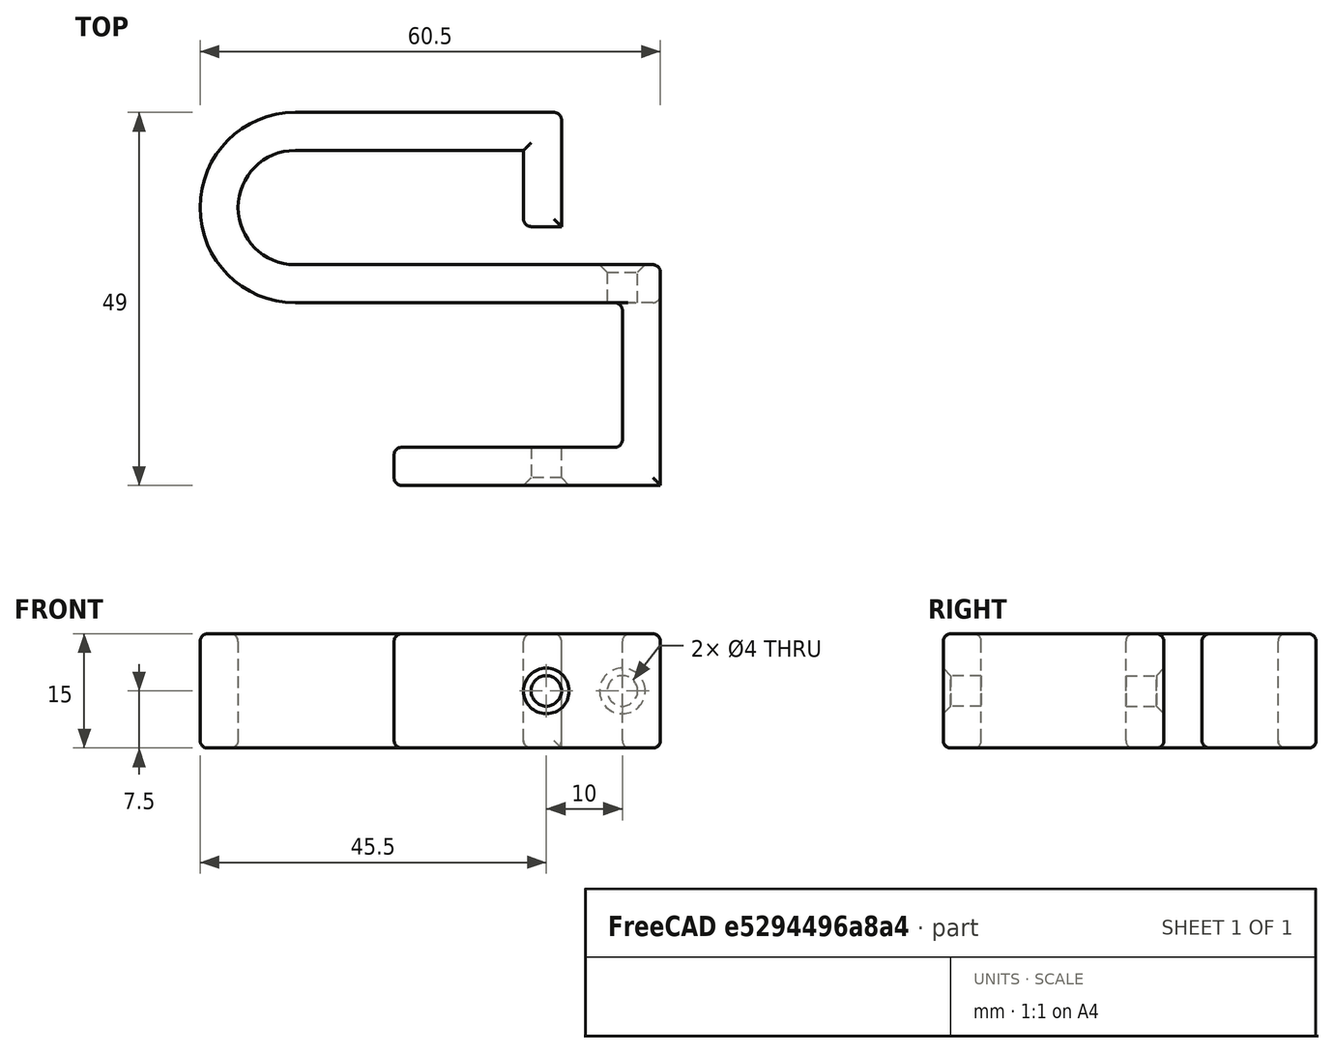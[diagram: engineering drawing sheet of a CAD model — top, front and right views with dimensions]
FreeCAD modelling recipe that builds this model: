
FCSTD DOCUMENT  (FreeCAD 0.21R33771 (Git))
Label: CableClip
License: All rights reserved
LicenseURL: http://en.wikipedia.org/wiki/All_rights_reserved
objects: Sketcher::SketchObject×4, PartDesign::Pad×2, PartDesign::Pocket×2, PartDesign::Chamfer×2, PartDesign::Fillet×2, PartDesign::Body×2, Mesh::Feature×2
note: 22 computed .brp shape members not serialized (recipe doc carries the construction recipe); baked Part::Feature solids carry a one-line shape summary decoded from their .brp

FEATURE [Sketcher::SketchObject] Sketch
  FullyConstrained = true
  MapMode = 5
  Support = -> [XY_Plane]
  sketch-geometry (10):
    g0: LineSegment StartX=13 StartY=-10 StartZ=0 EndX=-35 EndY=-10 EndZ=0
    g1: LineSegment StartX=-35 StartY=15 StartZ=0 EndX=0 EndY=15 EndZ=0
    g2: LineSegment StartX=0 StartY=15 StartZ=0 EndX=0 EndY=0 EndZ=0
    g3: ArcOfCircle CenterX=-35 CenterY=2.5 CenterZ=0 NormalX=0 NormalY=0 NormalZ=1 AngleXU=0 Radius=12.5 StartAngle=1.5708 EndAngle=4.71239
    g4: LineSegment StartX=0 StartY=0 StartZ=0 EndX=-5 EndY=0 EndZ=0
    g5: LineSegment StartX=-5 StartY=0 StartZ=0 EndX=-5 EndY=10 EndZ=0
    g6: LineSegment StartX=-5 StartY=10 StartZ=0 EndX=-35 EndY=10 EndZ=0
    g7: LineSegment StartX=-35 StartY=-5 StartZ=0 EndX=13 EndY=-5 EndZ=0
    g8: LineSegment StartX=13 StartY=-5 StartZ=0 EndX=13 EndY=-10 EndZ=0
    g9: ArcOfCircle CenterX=-35 CenterY=2.5 CenterZ=0 NormalX=0 NormalY=0 NormalZ=1 AngleXU=0 Radius=7.5 StartAngle=1.5708 EndAngle=4.71239
  constraints (31):
    c: Horizontal(g0)
    c: Horizontal(g1)
    c: Coincident(g1,g2)
    c: Coincident(g3,g0)
    c: DistanceX(g0,g0) = 48
    c: DistanceX(g1,g1) = 35
    c: Coincident(g3,g1)
    c: Diameter(g3) = 25
    c: Vertical(g1,g3)
    c: Vertical(g3,g0)
    c: Vertical(g2)
    c: DistanceY(g2,g2) = 15
    c: Coincident(g4,g5)
    c: Coincident(g5,g6)
    c: Horizontal(g6)
    c: Horizontal(g7)
    c: Coincident(g7,g8)
    c: Coincident(g8,g0)
    c: Vertical(g8)
    c: Coincident(g9,g6)
    c: Diameter(g9) = 15
    c: Coincident(g9,g7)
    c: Coincident(g2,g-1)
    c: Coincident(g4,g2)
    c: Horizontal(g4)
    c: DistanceX(g4,g4) = 5
    c: Vertical(g5,g4)
    c: DistanceY(g5,g1) = 5
    c: DistanceY(g0,g7) = 5
    c: Vertical(g0,g7)
    c: Vertical(g7,g6)
FEATURE [PartDesign::Pad] Pad
  Direction = (0,0,1)
  Length = 15
  Length2 = 10
  Profile = -> Sketch
  ReferenceAxis = -> Sketch [N_Axis]
  Type = 0
FEATURE [Sketcher::SketchObject] Sketch001
  ExternalGeometry = -> [Pad]
  FullyConstrained = true
  MapMode = 5
  Placement = pos=(0,-5,0) rot=(0,0.707107,0.707107;3.14159rad)
  Support = -> [Pad]
  sketch-geometry (1):
    g0: Circle CenterX=-8 CenterY=7.5 CenterZ=0 NormalX=0 NormalY=0 NormalZ=1 AngleXU=0 Radius=2
  constraints (3):
    c: Diameter(g0) = 4
    c: DistanceY(g-3,g0) = 7.5
    c: DistanceX(g-3,g0) = 5
FEATURE [PartDesign::Pocket] Pocket
  BaseFeature = -> Pad
  Direction = (0,-1,2e-16)
  Length = 5
  Length2 = 5
  Profile = -> Sketch001
  ReferenceAxis = -> Sketch001 [N_Axis]
  Type = 0
FEATURE [PartDesign::Chamfer] Chamfer
  Angle = 45
  Base = -> Pocket [Edge27]
  BaseFeature = -> Pocket
  ChamferType = 0
  FlipDirection = false
  Size = 1
  Size2 = 1
  SupportTransform = false
  UseAllEdges = false
FEATURE [PartDesign::Fillet] Fillet
  Base = -> Chamfer [Edge7,Edge14,Edge11,Edge21,Edge20,Edge19,Edge18,Edge13,Edge12,Edge17,Edge32,Edge24,Edge16,Edge22,Edge23,Edge28,Edge29,Edge27,Edge26,Edge25,Edge15,Edge8,Edge34,Edge33,Edge6]
  BaseFeature = -> Chamfer
  Radius = 1
  Refine = true
  SupportTransform = false
  UseAllEdges = false
FEATURE [PartDesign::Body] Body
  Group = -> [Sketch,Pad,Sketch001,Pocket,Chamfer,Fillet]
  Origin = -> Origin
  Tip = -> Fillet
FEATURE [Mesh::Feature] Mesh  label="Body (Meshed)"
FEATURE [Sketcher::SketchObject] Sketch002
  FullyConstrained = true
  MapMode = 5
  Support = -> [XY_Plane001]
  sketch-geometry (14):
    g0: LineSegment StartX=-35 StartY=15 StartZ=0 EndX=0 EndY=15 EndZ=0
    g1: LineSegment StartX=0 StartY=15 StartZ=0 EndX=0 EndY=0 EndZ=0
    g2: ArcOfCircle CenterX=-35 CenterY=2.5 CenterZ=0 NormalX=0 NormalY=0 NormalZ=1 AngleXU=0 Radius=12.5 StartAngle=1.5708 EndAngle=4.71239
    g3: LineSegment StartX=0 StartY=0 StartZ=0 EndX=-5 EndY=0 EndZ=0
    g4: LineSegment StartX=-5 StartY=0 StartZ=0 EndX=-5 EndY=10 EndZ=0
    g5: LineSegment StartX=-5 StartY=10 StartZ=0 EndX=-35 EndY=10 EndZ=0
    g6: LineSegment StartX=-35 StartY=-5 StartZ=0 EndX=13 EndY=-5 EndZ=0
    g7: LineSegment StartX=13 StartY=-5 StartZ=0 EndX=13 EndY=-34 EndZ=0
    g8: ArcOfCircle CenterX=-35 CenterY=2.5 CenterZ=0 NormalX=0 NormalY=0 NormalZ=1 AngleXU=0 Radius=7.5 StartAngle=1.5708 EndAngle=4.71239
    g9: LineSegment StartX=13 StartY=-34 StartZ=0 EndX=-22 EndY=-34 EndZ=0
    g10: LineSegment StartX=-22 StartY=-34 StartZ=0 EndX=-22 EndY=-29 EndZ=0
    g11: LineSegment StartX=-22 StartY=-29 StartZ=0 EndX=8 EndY=-29 EndZ=0
    g12: LineSegment StartX=8 StartY=-29 StartZ=0 EndX=8 EndY=-10 EndZ=0
    g13: LineSegment StartX=8 StartY=-10 StartZ=0 EndX=-35 EndY=-10 EndZ=0
  constraints (43):
    c: Horizontal(g0)
    c: Coincident(g0,g1)
    c: Coincident(g2,g13)
    c: DistanceX(g13,g7) = 48
    c: DistanceX(g0,g0) = 35
    c: Coincident(g2,g0)
    c: Diameter(g2) = 25
    c: Vertical(g0,g2)
    c: Vertical(g2,g13)
    c: Vertical(g1)
    c: DistanceY(g1,g1) = 15
    c: Coincident(g3,g4)
    c: Coincident(g4,g5)
    c: Horizontal(g5)
    c: Horizontal(g6)
    c: Coincident(g6,g7)
    c: Coincident(g8,g5)
    c: Diameter(g8) = 15
    c: Coincident(g8,g6)
    c: Coincident(g1,g-1)
    c: Coincident(g3,g1)
    c: Horizontal(g3)
    c: DistanceX(g3,g3) = 5
    c: Vertical(g4,g3)
    c: DistanceY(g4,g0) = 5
    c: Vertical(g13,g6)
    c: Vertical(g6,g5)
    c: Horizontal(g9)
    c: Coincident(g9,g10)
    c: Coincident(g10,g11)
    c: Coincident(g11,g12)
    c: Vertical(g12)
    c: Horizontal(g11)
    c: Vertical(g10)
    c: Equal(g3,g10)
    c: DistanceX(g11,g9) = 5
    c: Coincident(g7,g9)
    c: DistanceY(g11,g12) = 19
    c: DistanceX(g10,g11) = 30
    c: Coincident(g12,g13)
    c: Horizontal(g13)
    c: DistanceY(g2,g6) = 5
    c: Vertical(g7)
FEATURE [PartDesign::Pad] Pad001
  Direction = (0,0,1)
  Length = 15
  Length2 = 10
  Profile = -> Sketch002
  ReferenceAxis = -> Sketch002 [N_Axis]
  Type = 0
FEATURE [Sketcher::SketchObject] Sketch003
  ExternalGeometry = -> [Pad001]
  FullyConstrained = true
  MapMode = 5
  Placement = pos=(0,-34,0) rot=(1,0,0;1.5708rad)
  Support = -> [Pad001]
  sketch-geometry (1):
    g0: Circle CenterX=-2 CenterY=7.5 CenterZ=0 NormalX=0 NormalY=0 NormalZ=1 AngleXU=0 Radius=2
  constraints (3):
    c: Diameter(g0) = 4
    c: DistanceY(g-3,g0) = 7.5
    c: DistanceX(g0,g-3) = 15
FEATURE [PartDesign::Pocket] Pocket001
  BaseFeature = -> Pad001
  Direction = (0,1,-2e-16)
  Length = 5
  Length2 = 5
  Profile = -> Sketch003
  ReferenceAxis = -> Sketch003 [N_Axis]
  Type = 0
FEATURE [PartDesign::Fillet] Fillet001
  Base = -> Pocket001 [Edge42,Edge40,Edge28,Edge30,Edge19,Edge27,Edge31,Edge32,Edge7,Edge25,Edge6,Edge3,Edge4,Edge2,Edge10,Edge24,Edge14,Edge15,Edge23,Edge34,Edge38,Edge22,Face16,Edge29,Face14,Edge20,Edge13,Edge12,Edge11,Edge21,Edge17,Edge16]
  BaseFeature = -> Pocket001
  Radius = 1
  SupportTransform = false
  UseAllEdges = false
FEATURE [PartDesign::Chamfer] Chamfer001
  Angle = 45
  Base = -> Fillet001 [Edge133]
  BaseFeature = -> Fillet001
  ChamferType = 0
  FlipDirection = false
  Refine = true
  Size = 1
  Size2 = 1
  SupportTransform = false
  UseAllEdges = false
FEATURE [PartDesign::Body] Body001  label="ExtendedBody"
  Group = -> [Sketch002,Pad001,Sketch003,Pocket001,Fillet001,Chamfer001]
  Origin = -> Origin001
  Tip = -> Chamfer001
FEATURE [Mesh::Feature] Mesh001  label="ExtendedBody (Meshed)"
